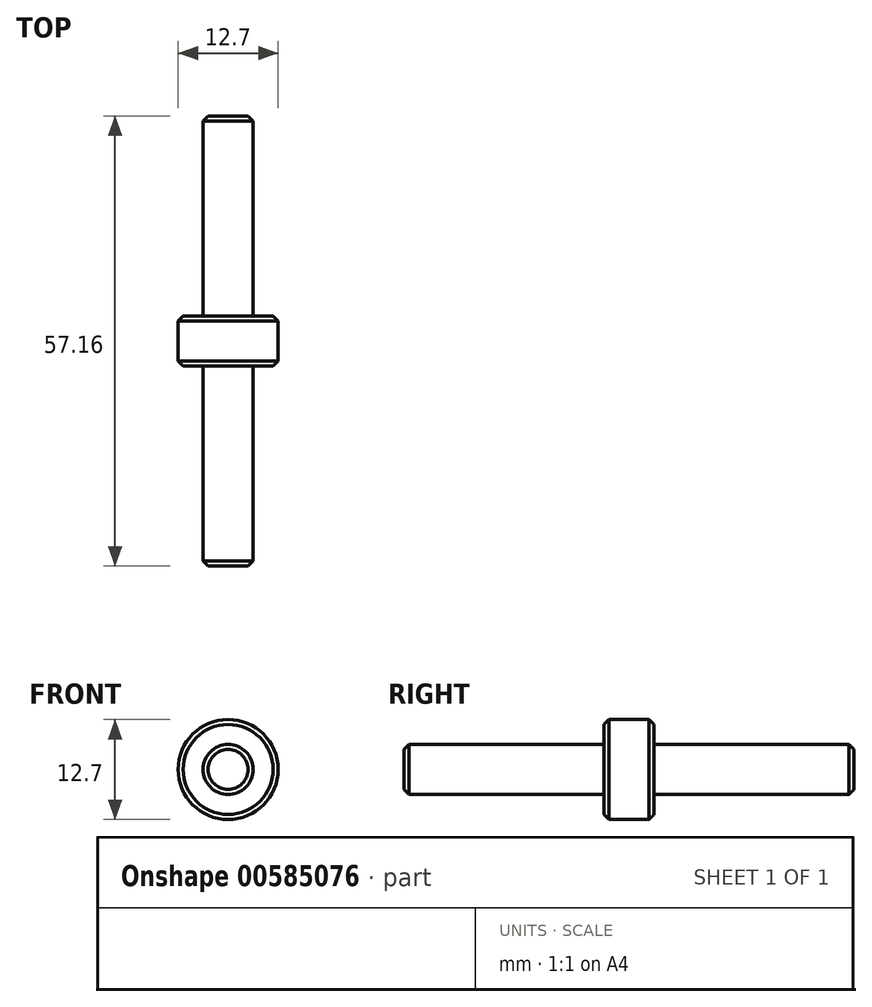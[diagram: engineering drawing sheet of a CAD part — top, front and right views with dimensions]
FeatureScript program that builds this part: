
annotation { "Feature Type Name" : "Feature", "Feature Type Description" : "" }
export const myFeature = defineFeature(function(context is Context, id is Id, definition is map)
    precondition{}
    {
        {
            var Q0;
            Q0=qCreatedBy(makeId("Front.planeOp"),FACE);
            var sketch = newSketch(context, id + "F0", { "sketchPlane" : qUnion([Q0])});
            skCircle(sketch, "E0", {"center": v(0, 0) * mm, "radius": 3.18 * mm});
            skCircle(sketch, "E1", {"center": v(0, 0) * mm, "radius": 6.35 * mm});
            skSolve(sketch);
        }
        {
            var Q0;
            Q0=makeQuery(id+"F0.imprint","IMPRINT",FACE,{"disambiguationData":[TD([[makeQuery(id+"F0.imprint","IMPRINT",EDGE,{"derivedFrom":sQuery(id+"F0.wireOp",EDGE,"E0")}),1.0]])]});
            extrude(context, id + "F1", {"entities" : qUnion([Q0]), "depth" : 57.15 * mm, "offsetDistance" : 25.4 * mm, "symmetric" : true});
        }
        {
            var Q0;
            Q0=makeQuery(id+"F0.imprint","IMPRINT",FACE,{"disambiguationData":[TD([[makeQuery(id+"F0.imprint","IMPRINT",EDGE,{"derivedFrom":sQuery(id+"F0.wireOp",EDGE,"E0")}),-1.0]])]});
            extrude(context, id + "F2", {"entities" : qUnion([Q0]), "operationType" : NewBodyOperationType.ADD, "depth" : 6.35 * mm, "offsetDistance" : 25.4 * mm, "symmetric" : true});
        }
        {
            var Q0;
            Q0=makeQuery(id+"F1.opExtrude","CAP_EDGE",EDGE,{"disambiguationData":[OSD([sQuery(id+"F0.wireOp",EDGE,"E0")])],"isStart":false});
            var Q1;
            Q1=makeQuery(id+"F1.opExtrude","CAP_EDGE",EDGE,{"disambiguationData":[OSD([sQuery(id+"F0.wireOp",EDGE,"E0")])],"isStart":true});
            var Q2;
            Q2=makeQuery(id+"F2.opExtrude","CAP_EDGE",EDGE,{"disambiguationData":[OSD([sQuery(id+"F0.wireOp",EDGE,"E1")])],"isStart":false});
            var Q3;
            Q3=makeQuery(id+"F2.opExtrude","CAP_EDGE",EDGE,{"disambiguationData":[OSD([sQuery(id+"F0.wireOp",EDGE,"E1")])],"isStart":true});
            chamfer(context, id + "F3", {"entities" : qUnion([Q0, Q1, Q2, Q3]), "width" : 0.64 * mm, "tangentPropagation" : true});
        }
    });
